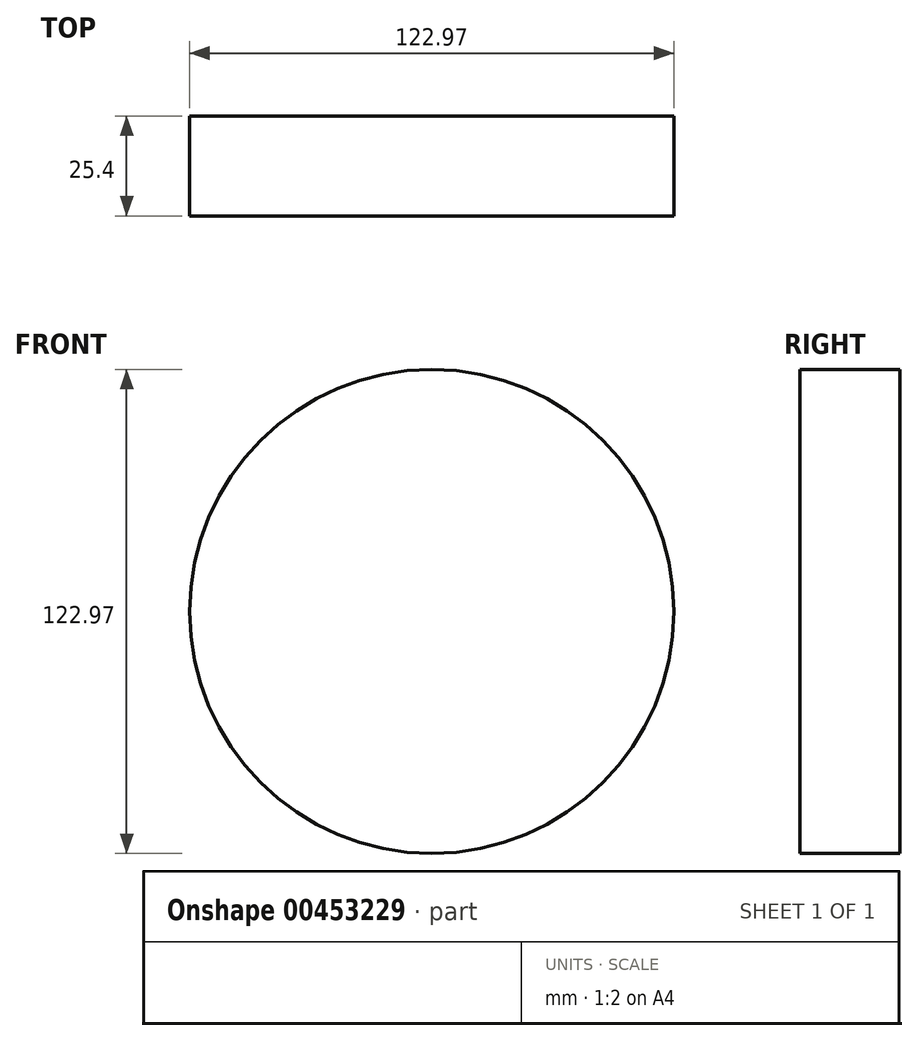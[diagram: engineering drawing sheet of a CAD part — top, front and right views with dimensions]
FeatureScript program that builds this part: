
annotation { "Feature Type Name" : "Feature", "Feature Type Description" : "" }
export const myFeature = defineFeature(function(context is Context, id is Id, definition is map)
    precondition{}
    {
        {
            var Q0;
            Q0=qCreatedBy(makeId("Front.planeOp"),FACE);
            var sketch = newSketch(context, id + "F0", { "sketchPlane" : qUnion([Q0])});
            skCircle(sketch, "E0", {"center": v(9.54, -38.01) * mm, "radius": 61.48 * mm});
            skSolve(sketch);
        }
        {
            var Q0;
            Q0=makeQuery(id+"F0.imprint","IMPRINT",FACE,{"disambiguationData":[TD([[makeQuery(id+"F0.imprint","IMPRINT",EDGE,{"derivedFrom":sQuery(id+"F0.wireOp",EDGE,"E0")}),1.0]])]});
            extrude(context, id + "F1", {"entities" : qUnion([Q0]), "depth" : 25.4 * mm});
        }
    });
